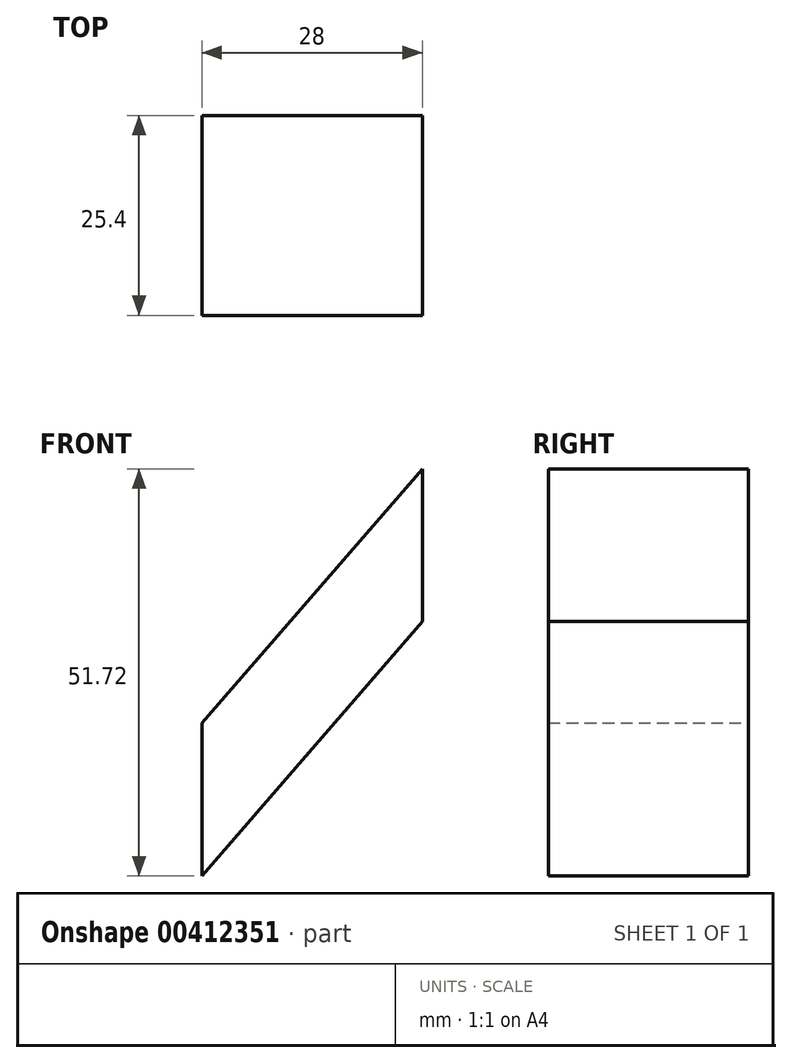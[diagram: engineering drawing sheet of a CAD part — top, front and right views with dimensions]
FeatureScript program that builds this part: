
annotation { "Feature Type Name" : "Feature", "Feature Type Description" : "" }
export const myFeature = defineFeature(function(context is Context, id is Id, definition is map)
    precondition{}
    {
        {
            var Q0;
            Q0=qCreatedBy(makeId("Front.planeOp"),FACE);
            var sketch = newSketch(context, id + "F0", { "sketchPlane" : qUnion([Q0])});
            skLineSegment(sketch, "E0", {"start": v(28, 32.29) * mm, "end": v(0, 0) * mm});
            skLineSegment(sketch, "E1", {"start": v(0, 0) * mm, "end": v(0, -19.43) * mm});
            skLineSegment(sketch, "E2", {"start": v(0, -19.43) * mm, "end": v(28, 12.88) * mm});
            skLineSegment(sketch, "E3", {"start": v(28, 12.88) * mm, "end": v(28, 32.29) * mm});
            skSolve(sketch);
        }
        {
            var Q0;
            Q0 = qSketchRegion(id + "F0", true);
            extrude(context, id + "F1", {"entities" : qUnion([Q0]), "depth" : 25.4 * mm});
        }
    });
